# Revit family: ALBA_R200ExSWxxSF
name_source: partatom
category: Leuchten
units: mm (PartAtom-declared; Revit-internal decimal feet)

## family parameters
Basisbauteil = Fläche
Beim Laden mit Abzugskörper schneiden = Nein
Bemaßung runder Anschluss = Durchmesser verwenden
Gemeinsam genutzt = Nein
Lichtquelle = Ja
OmniClass-Nummer = 23.80.70.11
OmniClass-Titel = Luminaries for Internal Lighting
Raumberechnungspunkt = Nein
Teiletyp = Normal

## types (16) — shared parameters
Baugruppenkennzeichen = D5020200
Datei für fotometrisches Netz = Master_ALBA_R200E_SW_Diffusor.IES
Emissionsform beim Rendern sichtbar = Nein
Farbfilter = 16777215
Farbtemperaturverschiebung bei Dämpfen der Lampe = <Keine Auswahl>
Hersteller = RIDI Leuchten GmbH
Lampe = LED
Neigungswinkel = 90.00°
URL = www.ridi.de
Von Kreisdurchmesser aussenden = 182 mm  [stored 0.597113 ft]
brand = RIDI
conformity mark = CE
electrical safety class = 2
height = 101 mm  [stored 0.331365 ft]
ingress protection (IP) code = IP20
length = 208 mm
nominal frequency = 50-60Hz
nominal voltage = 230
voltage type (AC, DC, UC) = AC
weight = 0.81 kg
width = 208 mm
zero-valued in all types: Vorgabe-Ansicht

## per-type parameters (varying)
| type | Modell | Scheinlast | rated input power |
| ALBA R200E NDSW830SF0175OS | 0322149 | 17 VA | 17 |
| ALBA R200E NDSW840SF0175OS | 0322150 | 17 VA | 17 |
| ALBA R200E NDSW830SF0250OS | 0322161 | 26 VA | 26 |
| ALBA R200E NDSW840SF0250OS | 0322162 | 26 VA | 26 |
| ALBA R200E DASW830SF0175OS | 0332149 | 17 VA | 17 |
| ALBA R200E DASW840SF0175OS | 0332150 | 17 VA | 17 |
| ALBA R200E DASW830SF0250OS | 0332161 | 26 VA | 26 |
| ALBA R200E DASW840SF0250OS | 0332162 | 26 VA | 26 |
| ALBA R200E NDSW930SF0150OS | 0322398 | 17 VA | 17 |
| ALBA R200E DASW930SF0150OS | 0332398 | 17 VA | 17 |
| ALBA R200E NDSW930SF0200OS | 0322434 | 26 VA | 26 |
| ALBA R200E DASW930SF0200OS | 0332434 | 26 VA | 26 |
| ALBA R200E DASW940SF0150OS | 0332399 | 17 VA | 17 |
| ALBA R200E NDSW940SF0150OS | 0322399 | 17 VA | 17 |
| ALBA R200E NDSW940SF0225OS | 0322435 | 26 VA | 26 |
| ALBA R200E DASW940SF0225OS | 0332435 | 26 VA | 26 |

note: column(s) folded — value = type name in every type: product name

note: [stored X ft] marks values corroborated as IEEE doubles in the binary element streams (Revit-internal decimal feet)
